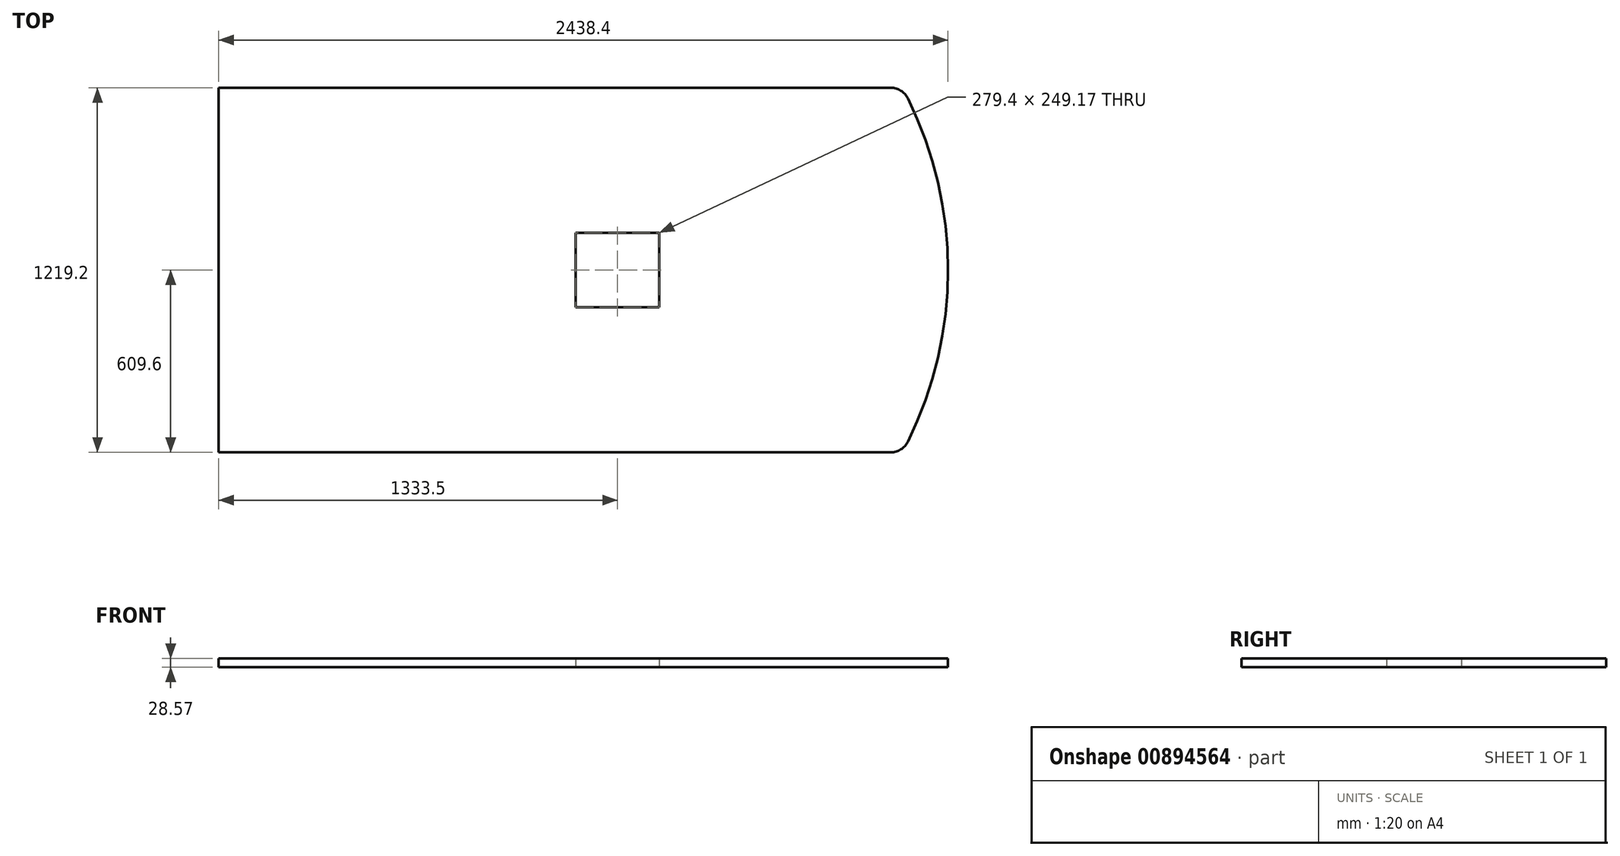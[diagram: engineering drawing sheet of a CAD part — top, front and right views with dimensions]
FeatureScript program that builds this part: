
annotation { "Feature Type Name" : "Feature", "Feature Type Description" : "" }
export const myFeature = defineFeature(function(context is Context, id is Id, definition is map)
    precondition{}
    {
        {
            var Q0;
            Q0=qCreatedBy(makeId("Top.planeOp"),FACE);
            var sketch = newSketch(context, id + "F0", { "sketchPlane" : qUnion([Q0])});
            skLineSegment(sketch, "E0.bottom", {"start": v(-1143, 609.6) * mm, "end": v(1104.24, 609.6) * mm});
            skLineSegment(sketch, "E0.top", {"start": v(-1143, -609.6) * mm, "end": v(1104.24, -609.6) * mm});
            skLineSegment(sketch, "E0.left", {"start": v(-1143, 609.6) * mm, "end": v(-1143, -609.6) * mm});
            skPoint(sketch, "E0.middle", {"position": v(0, 0) * mm});
            skLineSegment(sketch, "E1", {"start": v(1143, 0) * mm, "end": v(1295.4, 0) * mm});
            skArc(sketch, "E2", {"start": v(1161.16, -574.25) * mm, "mid": v(1295.4, 0) * mm, "end": v(1161.16, 574.25) * mm});
            skPoint(sketch, "E3.visualSharp", {"position": v(1143, 609.6) * mm});
            skArc(sketch, "E3.filletArc", {"start": v(1161.16, 574.25) * mm, "mid": v(1137.74, 600.04) * mm, "end": v(1104.24, 609.6) * mm});
            skPoint(sketch, "E4.visualSharp", {"position": v(1143, -609.6) * mm});
            skArc(sketch, "E4.filletArc", {"start": v(1104.24, -609.6) * mm, "mid": v(1137.74, -600.04) * mm, "end": v(1161.16, -574.25) * mm});
            skLineSegment(sketch, "E5", {"start": v(1143, 0) * mm, "end": v(-1143, 0) * mm});
            skLineSegment(sketch, "E6", {"start": v(1295.4, 0) * mm, "end": v(190.5, 0) * mm});
            skLineSegment(sketch, "E7.bottom", {"start": v(330.2, 124.59) * mm, "end": v(50.8, 124.59) * mm});
            skLineSegment(sketch, "E7.top", {"start": v(330.2, -124.59) * mm, "end": v(50.8, -124.59) * mm});
            skLineSegment(sketch, "E7.left", {"start": v(330.2, 124.59) * mm, "end": v(330.2, -124.59) * mm});
            skLineSegment(sketch, "E7.right", {"start": v(50.8, 124.59) * mm, "end": v(50.8, -124.59) * mm});
            skPoint(sketch, "E7.middle", {"position": v(190.5, 0) * mm});
            skSolve(sketch);
        }
        {
            var Q0;
            {var subQ2=sQuery(id+"F0.wireOp",EDGE,"bponJt8q-Vroz-T6uM-5gtj-sUBrWClouF9q");Q0=makeQuery(id+"F0.imprint","IMPRINT",FACE,{"disambiguationData":[TD([[makeQuery(id+"F0.imprint","IMPRINT",EDGE,{"derivedFrom":subQ2}),1.0]])]});}
            var Q1;
            {var subQ1=sQuery(id+"F0.wireOp",EDGE,"s5ovrSA8-h5CN-1mHA-tY9A-8cbjFLr5iEL2");Q1=makeQuery(id+"F0.imprint","IMPRINT",FACE,{"disambiguationData":[TD([[makeQuery(id+"F0.imprint","IMPRINT",EDGE,{"derivedFrom":subQ1}),-1.0]])]});}
            var Q2;
            Q2=makeQuery(id+"F0.imprint","IMPRINT",FACE,{"disambiguationData":[TD([[makeQuery(id+"F0.imprint","IMPRINT",EDGE,{"derivedFrom":sQuery(id+"F0.wireOp",EDGE,"E0.bottom")}),-1.0]])]});
            var Q3;
            {var subQ0=sQuery(id+"F0.wireOp",EDGE,"E1");Q3=makeQuery(id+"F0.imprint","IMPRINT",FACE,{"disambiguationData":[TD([[makeQuery(id+"F0.imprint","IMPRINT",EDGE,{"derivedFrom":subQ0}),-1.0]])]});}
            var Q4;
            {var subQ4=sQuery(id+"F0.wireOp",EDGE,"E0.top");Q4=makeQuery(id+"F0.imprint","IMPRINT",FACE,{"disambiguationData":[TD([[makeQuery(id+"F0.imprint","IMPRINT",EDGE,{"derivedFrom":subQ4}),1.0]])]});}
            extrude(context, id + "F1", {"entities" : qUnion([Q0, Q1, Q2, Q3, Q4]), "depth" : 28.57 * mm, "offsetDistance" : 25.4 * mm});
        }
    });
